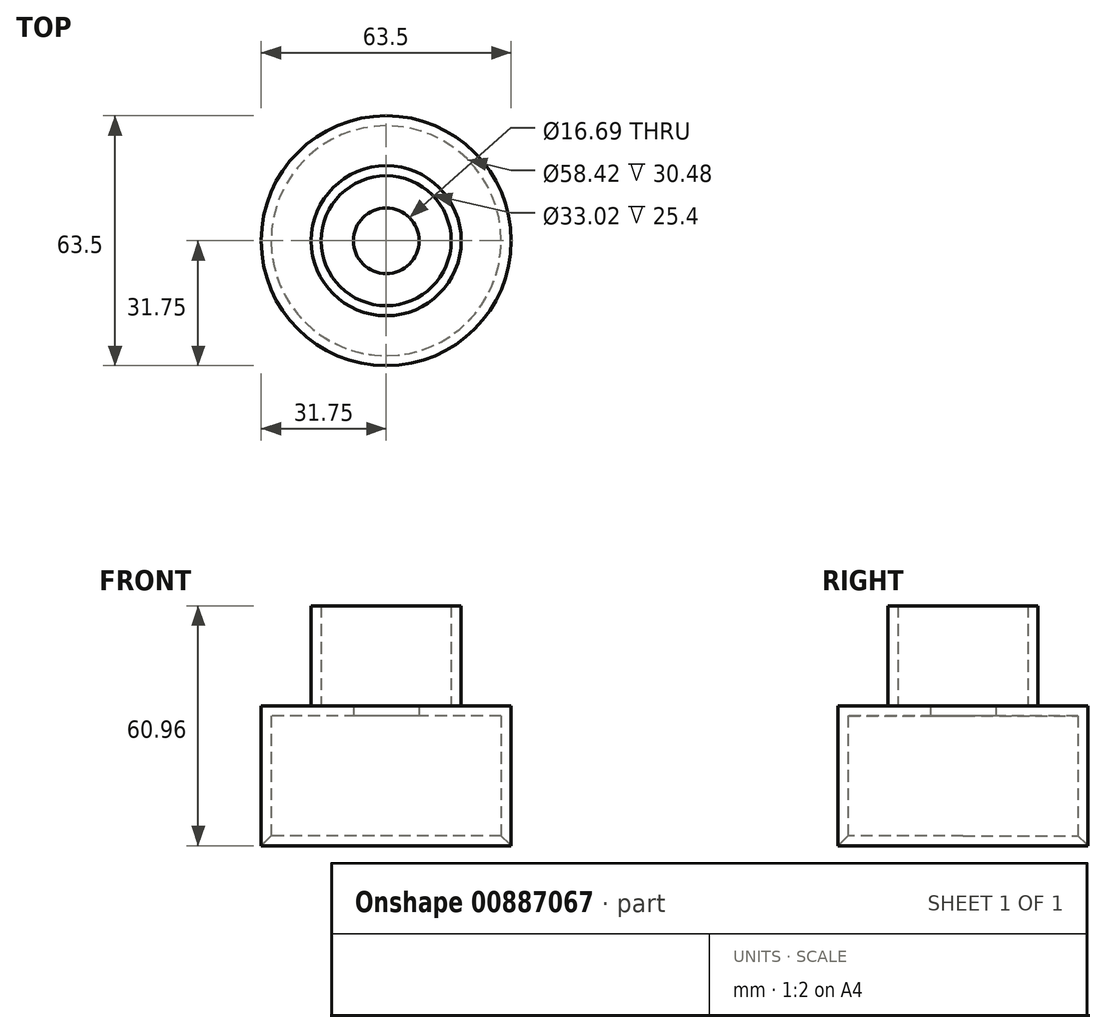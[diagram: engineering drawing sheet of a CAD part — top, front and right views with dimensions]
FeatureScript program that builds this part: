
annotation { "Feature Type Name" : "Feature", "Feature Type Description" : "" }
export const myFeature = defineFeature(function(context is Context, id is Id, definition is map)
    precondition{}
    {
        {
            var Q0;
            Q0=qCreatedBy(makeId("Top.planeOp"),FACE);
            var sketch = newSketch(context, id + "F0", { "sketchPlane" : qUnion([Q0])});
            skCircle(sketch, "E0", {"center": v(0, 0) * mm, "radius": 31.75 * mm});
            skCircle(sketch, "E1", {"center": v(0, 0) * mm, "radius": 8.35 * mm});
            skSolve(sketch);
        }
        {
            var Q0;
            Q0=makeQuery(id+"F0.imprint","IMPRINT",FACE,{"disambiguationData":[TD([[makeQuery(id+"F0.imprint","IMPRINT",EDGE,{"derivedFrom":sQuery(id+"F0.wireOp",EDGE,"E0")}),1.0]])]});
            extrude(context, id + "F1", {"entities" : qUnion([Q0]), "depth" : 38.1 * mm, "offsetDistance" : 25.4 * mm});
        }
        {
            var Q0;
            Q0=makeQuery(id+"F1.opExtrude","CAP_FACE",FACE,{"disambiguationData":[OSD([sQuery(id+"F0.wireOp",EDGE,"E0"),sQuery(id+"F0.wireOp",EDGE,"E1")])],"isStart":true});
            var Q1;
            Q1=makeQuery(id+"F1.opExtrude","SWEPT_FACE",FACE,{"disambiguationData":[OSD([sQuery(id+"F0.wireOp",EDGE,"E1")])]});
            shell(context, id + "F2", {"entities" : qUnion([Q0, Q1]), "thickness" : 2.54 * mm});
        }
        {
            var Q0;
            Q0=makeQuery(id+"F1.opExtrude","CAP_FACE",FACE,{"disambiguationData":[OSD([sQuery(id+"F0.wireOp",EDGE,"E0"),sQuery(id+"F0.wireOp",EDGE,"E1")])],"isStart":false});
            var sketch = newSketch(context, id + "F3", { "sketchPlane" : qUnion([Q0])});
            skCircle(sketch, "E2", {"center": v(0, 0) * mm, "radius": 19.05 * mm});
            skSolve(sketch);
        }
        {
            var Q0;
            Q0=makeQuery(id+"F3.imprint","IMPRINT",FACE,{"disambiguationData":[TD([[makeQuery(id+"F3.imprint","IMPRINT",EDGE,{"derivedFrom":sQuery(id+"F3.wireOp",EDGE,"E2")}),1.0]])]});
            var Q1;
            Q1=sQuery(id+"F3.wireOp",EDGE,"E2");
            extrude(context, id + "F4", {"entities" : qUnion([Q0]), "operationType" : NewBodyOperationType.ADD, "surfaceEntities" : qUnion([Q1]), "depth" : 25.4 * mm, "offsetDistance" : 25.4 * mm});
        }
        {
            var Q0;
            Q0=makeQuery(id+"F1.opExtrude","CAP_EDGE",EDGE,{"disambiguationData":[OSD([sQuery(id+"F0.wireOp",EDGE,"E0")])],"isStart":false});
            var Q1;
            Q1=makeQuery(id+"F4.opExtrude","CAP_EDGE",EDGE,{"disambiguationData":[OSD([sQuery(id+"F3.wireOp",EDGE,"E2")])],"isStart":false});
            loft(context, id + "F5", {"bodyType" : ToolBodyType.SURFACE, "wireProfilesArray" : [{ "wireProfileEntities" : qUnion([Q0]) }, { "wireProfileEntities" : qUnion([Q1]) }]});
        }
        {
            var Q0;
            Q0=makeQuery(id+"F4.opExtrude","CAP_FACE",FACE,{"disambiguationData":[OSD([sQuery(id+"F0.wireOp",EDGE,"E1"),sQuery(id+"F3.wireOp",EDGE,"E2")])],"isStart":false});
            var Q1;
            {var subQ0=sQuery(id+"F0.wireOp",EDGE,"E1");Q1=makeQuery(id+"F4.boolean.opBoolean","MERGE",FACE,{"derivedFrom":[makeQuery(id+"F1.opExtrude","SWEPT_FACE",FACE,{"disambiguationData":[OSD([subQ0])]}),makeQuery(id+"F4.opExtrude","SWEPT_FACE",FACE,{"disambiguationData":[OSD([subQ0])]})]});}
            shell(context, id + "F6", {"entities" : qUnion([Q0, Q1]), "thickness" : 2.54 * mm});
        }
        {
            var Q0;
            {var subQ0=sQuery(id+"F0.wireOp",EDGE,"E0");Q0=makeQuery(id+"F2.opShell","OFFSET_EDGE",EDGE,{"disambiguationData":[OSD([subQ0]),TDD([makeQuery(id+"F1.opExtrude","CAP_EDGE",EDGE,{"disambiguationData":[OSD([subQ0])],"isStart":true})])]});}
            chamfer(context, id + "F7", {"entities" : qUnion([Q0]), "width" : 5.08 * mm, "tangentPropagation" : true});
        }
    });
